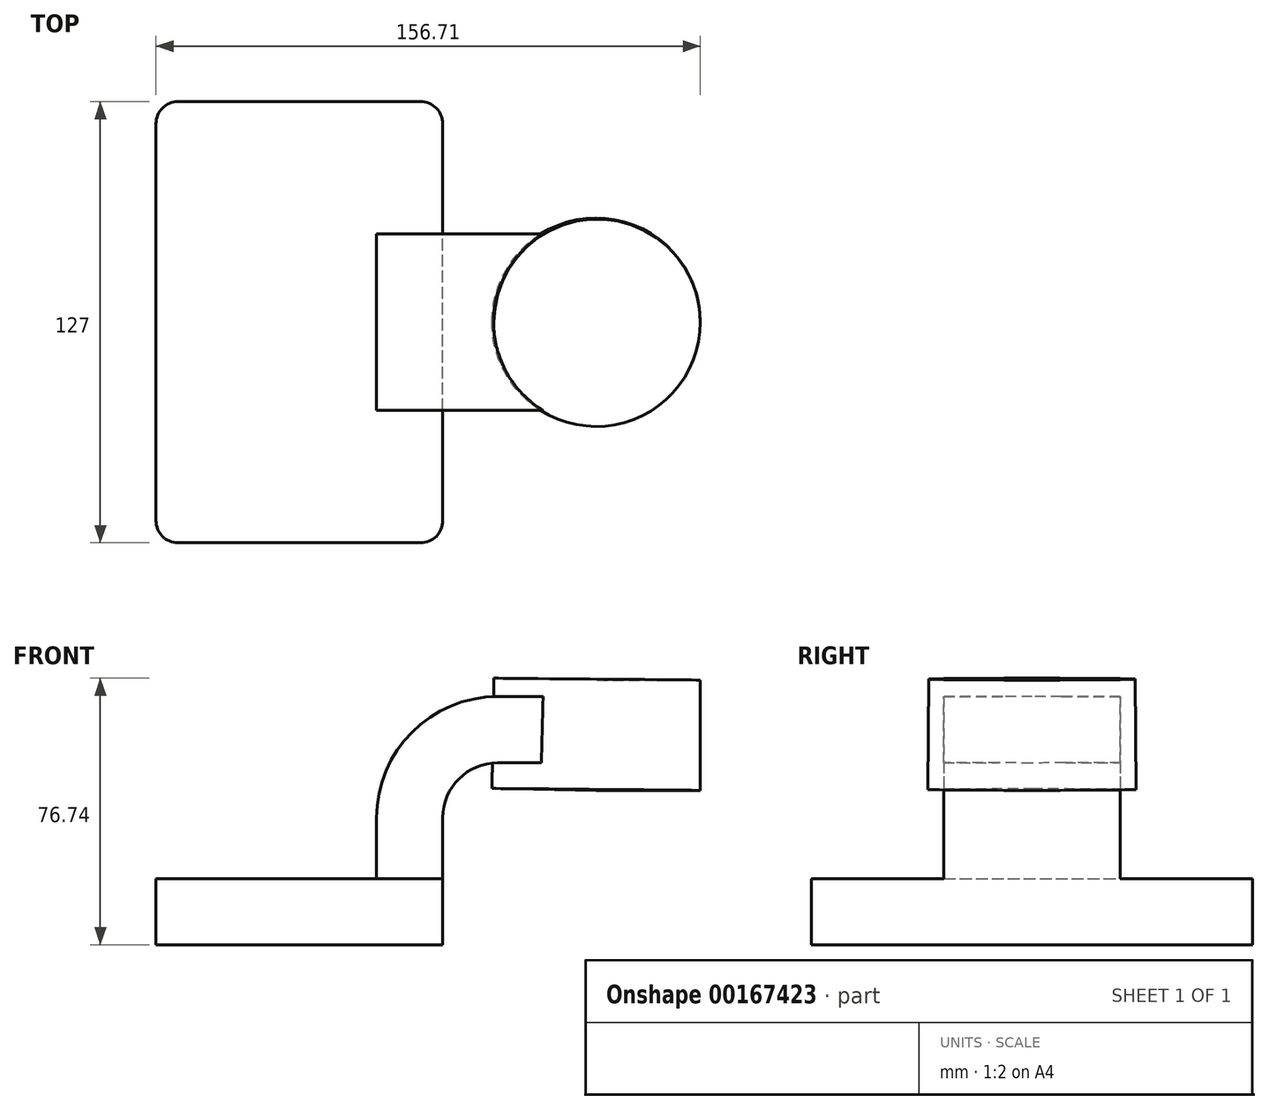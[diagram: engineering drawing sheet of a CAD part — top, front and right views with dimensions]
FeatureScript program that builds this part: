
annotation { "Feature Type Name" : "Feature", "Feature Type Description" : "" }
export const myFeature = defineFeature(function(context is Context, id is Id, definition is map)
    precondition{}
    {
        {
            var Q0;
            Q0=qCreatedBy(makeId("Front.planeOp"),FACE);
            var sketch = newSketch(context, id + "F0", { "sketchPlane" : qUnion([Q0])});
            skLineSegment(sketch, "E0.bottom", {"start": v(0, 0) * mm, "end": v(82.55, 0) * mm});
            skLineSegment(sketch, "E0.top", {"start": v(0, 19.05) * mm, "end": v(82.55, 19.05) * mm});
            skLineSegment(sketch, "E0.left", {"start": v(0, 0) * mm, "end": v(0, 19.05) * mm});
            skLineSegment(sketch, "E0.right", {"start": v(82.55, 0) * mm, "end": v(82.55, 19.05) * mm});
            skLineSegment(sketch, "E1", {"start": v(82.55, 19.05) * mm, "end": v(82.55, 36.53) * mm});
            skArc(sketch, "E2", {"start": v(82.55, 36.53) * mm, "mid": v(87.2, 47.75) * mm, "end": v(98.43, 52.4) * mm});
            skLineSegment(sketch, "E3", {"start": v(98.43, 52.4) * mm, "end": v(127, 52.4) * mm});
            skLineSegment(sketch, "E4.bottom", {"start": v(105.91, 76.2) * mm, "end": v(156.71, 76.2) * mm});
            skLineSegment(sketch, "E4.top", {"start": v(105.91, 44.45) * mm, "end": v(156.71, 44.45) * mm});
            skLineSegment(sketch, "E4.left", {"start": v(105.91, 76.2) * mm, "end": v(105.91, 44.45) * mm});
            skLineSegment(sketch, "E4.right", {"start": v(156.71, 76.2) * mm, "end": v(156.71, 44.45) * mm});
            skLineSegment(sketch, "E5.0", {"start": v(98.43, 71.45) * mm, "end": v(127, 71.45) * mm});
            skArc(sketch, "E5.1", {"start": v(63.5, 36.53) * mm, "mid": v(73.73, 61.22) * mm, "end": v(98.43, 71.45) * mm});
            skLineSegment(sketch, "E6.0", {"start": v(63.5, 19.05) * mm, "end": v(63.5, 36.53) * mm});
            skLineSegment(sketch, "E7", {"start": v(126.71, 44.45) * mm, "end": v(127, 76.2) * mm});
            skFitSpline(sketch, "E8", {"points": [v(98.43, 71.45) * mm, v(0, 19.05) * mm], "startDerivative": vector(-187.89, 0) * mm, "endDerivative": vector(-47.33, -110.9) * mm});
            skSolve(sketch);
        }
        {
            var Q0;
            Q0=makeQuery(id+"F0.imprint","IMPRINT",FACE,{"disambiguationData":[TD([[makeQuery(id+"F0.imprint","IMPRINT",EDGE,{"derivedFrom":sQuery(id+"F0.wireOp",EDGE,"E0.bottom")}),1.0]])]});
            extrude(context, id + "F1", {"entities" : qUnion([Q0]), "endBound" : BoundingType.SYMMETRIC, "depth" : 127 * mm});
        }
        {
            var Q0;
            {var subQ7=sQuery(id+"F0.wireOp",EDGE,"E1");Q0=makeQuery(id+"F0.imprint","IMPRINT",FACE,{"disambiguationData":[TD([[makeQuery(id+"F0.imprint","IMPRINT",EDGE,{"derivedFrom":subQ7}),1.0]])]});}
            var Q1;
            {var subQ0=sQuery(id+"F0.wireOp",EDGE,"E4.left");var subQ1=sQuery(id+"F0.wireOp",EDGE,"E3");var subQ2=makeQuery(id+"F0.imprint","INTERSECT",VERTEX,{"derivedFrom":[subQ1,subQ0]});Q1=makeQuery(id+"F0.imprint","IMPRINT",FACE,{"disambiguationData":[TD([[makeQuery(id+"F0.imprint","IMPRINT",EDGE,{"disambiguationData":[TD([[subQ2,-1.0]])],"derivedFrom":subQ1}),1.0]])]});}
            extrude(context, id + "F2", {"entities" : qUnion([Q0, Q1]), "operationType" : NewBodyOperationType.ADD, "endBound" : BoundingType.SYMMETRIC, "depth" : 50.8 * mm});
        }
        {
            var Q0;
            Q0=makeQuery(id+"F0.imprint","IMPRINT",FACE,{"disambiguationData":[TD([[makeQuery(id+"F0.imprint","IMPRINT",EDGE,{"derivedFrom":sQuery(id+"F0.wireOp",EDGE,"E5.1")}),1.0]])]});
            extrude(context, id + "F3", {"entities" : qUnion([Q0]), "operationType" : NewBodyOperationType.ADD, "endBound" : BoundingType.SYMMETRIC, "depth" : 15.88 * mm});
        }
        {
            var Q0;
            {var subQ4=sQuery(id+"F0.wireOp",EDGE,"E4.right");Q0=makeQuery(id+"F0.imprint","IMPRINT",FACE,{"disambiguationData":[TD([[makeQuery(id+"F0.imprint","IMPRINT",EDGE,{"derivedFrom":subQ4}),-1.0]])]});}
            var Q1;
            Q1=sQuery(id+"F0.wireOp",EDGE,"E7");
            revolve(context, id + "F4", {"operationType" : NewBodyOperationType.ADD, "entities" : qUnion([Q0]), "axis" : qUnion([Q1]), "revolveType" : RevolveType.FULL});
        }
        {
            var Q0;
            Q0=makeQuery(id+"F1.opExtrude","CAP_EDGE",EDGE,{"disambiguationData":[OSD([sQuery(id+"F0.wireOp",EDGE,"E0.left")])],"isStart":false});
            var Q1;
            Q1=makeQuery(id+"F1.opExtrude","CAP_EDGE",EDGE,{"disambiguationData":[OSD([sQuery(id+"F0.wireOp",EDGE,"E0.right")])],"isStart":false});
            var Q2;
            Q2=makeQuery(id+"F1.opExtrude","CAP_EDGE",EDGE,{"disambiguationData":[OSD([sQuery(id+"F0.wireOp",EDGE,"E0.right")])],"isStart":true});
            var Q3;
            Q3=makeQuery(id+"F1.opExtrude","CAP_EDGE",EDGE,{"disambiguationData":[OSD([sQuery(id+"F0.wireOp",EDGE,"E0.left")])],"isStart":true});
            fillet(context, id + "F5", {"entities" : qUnion([Q0, Q1, Q2, Q3]), "radius" : 6.35 * mm, "tangentPropagation" : true, "allowEdgeOverflow" : false});
        }
    });
